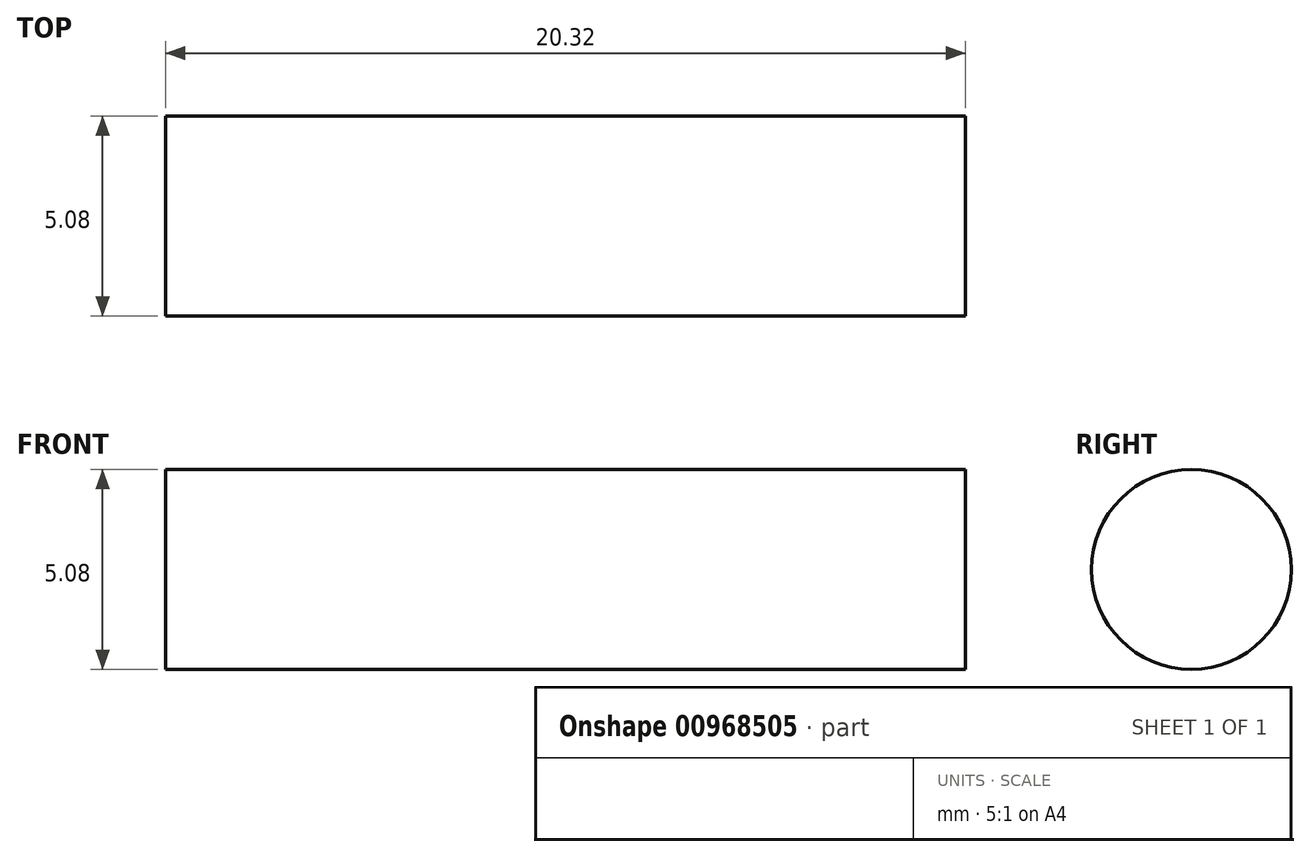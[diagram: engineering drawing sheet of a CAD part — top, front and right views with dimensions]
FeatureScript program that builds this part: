
annotation { "Feature Type Name" : "Feature", "Feature Type Description" : "" }
export const myFeature = defineFeature(function(context is Context, id is Id, definition is map)
    precondition{}
    {
        {
            var Q0;
            Q0=qCreatedBy(makeId("Right.planeOp"),FACE);
            var sketch = newSketch(context, id + "F0", { "sketchPlane" : qUnion([Q0])});
            skCircle(sketch, "E0", {"center": v(0, 0) * mm, "radius": 2.54 * mm});
            skSolve(sketch);
        }
        {
            var Q0;
            Q0=makeQuery(id+"F0.imprint","IMPRINT",FACE,{"disambiguationData":[TD([[makeQuery(id+"F0.imprint","IMPRINT",EDGE,{"derivedFrom":sQuery(id+"F0.wireOp",EDGE,"E0")}),1.0]])]});
            extrude(context, id + "F1", {"entities" : qUnion([Q0]), "depth" : 20.32 * mm, "offsetDistance" : 25.4 * mm});
        }
    });
